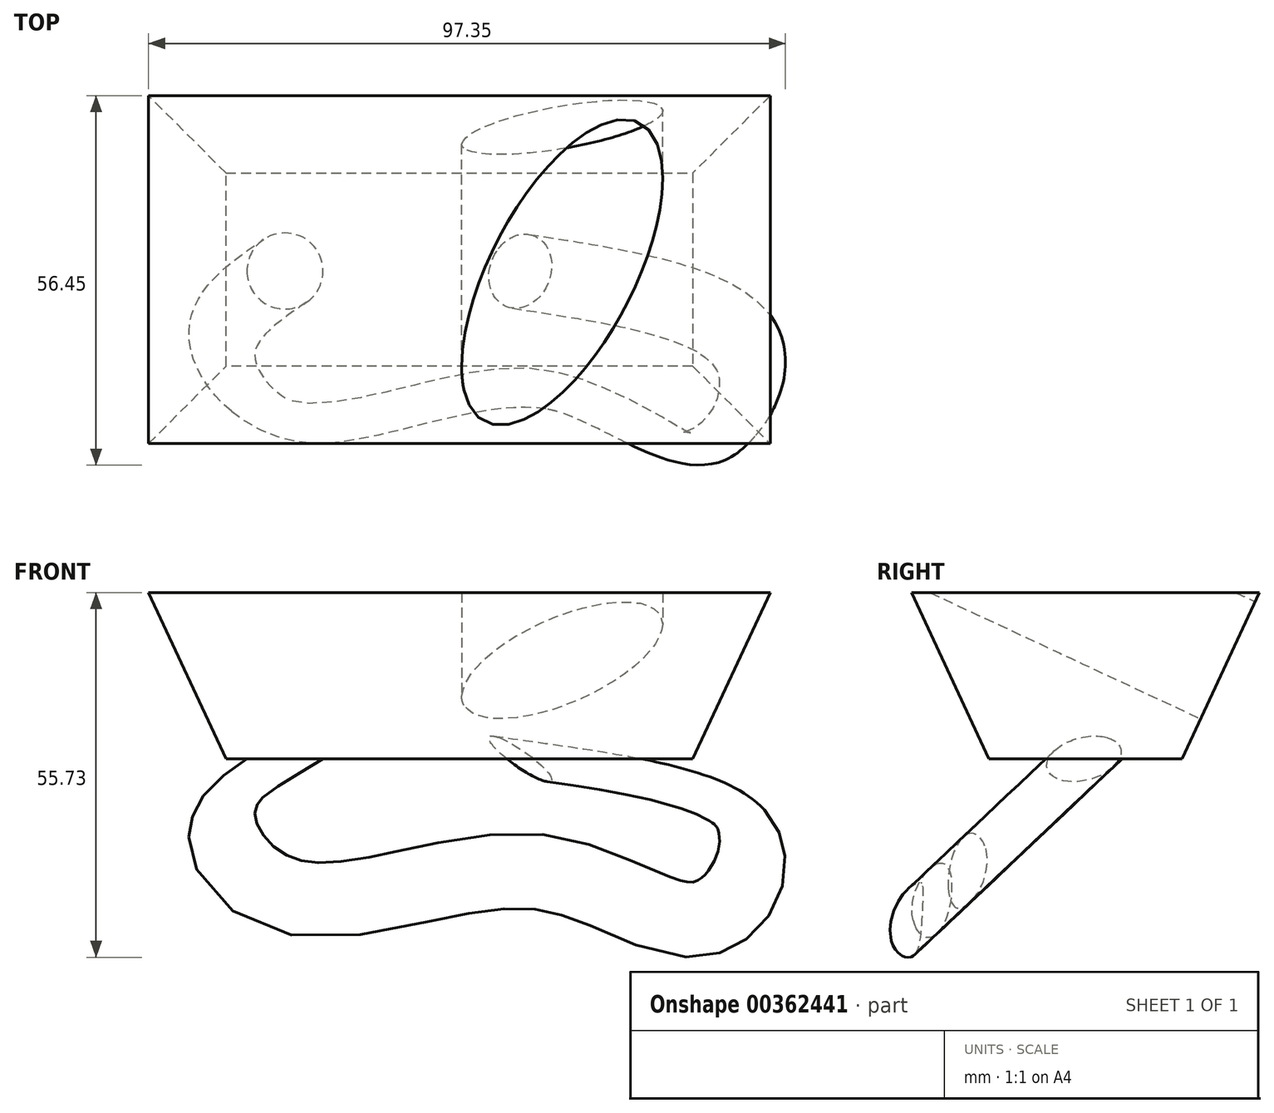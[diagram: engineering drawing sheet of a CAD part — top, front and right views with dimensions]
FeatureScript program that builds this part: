
annotation { "Feature Type Name" : "Feature", "Feature Type Description" : "" }
export const myFeature = defineFeature(function(context is Context, id is Id, definition is map)
    precondition{}
    {
        {
            var Q0;
            Q0=qCreatedBy(makeId("Top.planeOp"),FACE);
            var sketch = newSketch(context, id + "F0", { "sketchPlane" : qUnion([Q0])});
            skLineSegment(sketch, "E0.bottom", {"start": v(13.31, 11.56) * mm, "end": v(-58.01, 11.56) * mm});
            skLineSegment(sketch, "E0.top", {"start": v(13.31, 41.05) * mm, "end": v(-58.01, 41.05) * mm});
            skLineSegment(sketch, "E0.left", {"start": v(13.31, 11.56) * mm, "end": v(13.31, 41.05) * mm});
            skLineSegment(sketch, "E0.right", {"start": v(-58.01, 11.56) * mm, "end": v(-58.01, 41.05) * mm});
            skPoint(sketch, "E0.middle", {"position": v(-22.35, 26.3) * mm});
            skSolve(sketch);
        }
        {
            var Q0;
            Q0=makeQuery(id+"F0.imprint","IMPRINT",FACE,{"disambiguationData":[TD([[makeQuery(id+"F0.imprint","IMPRINT",EDGE,{"derivedFrom":sQuery(id+"F0.wireOp",EDGE,"E0.bottom")}),-1.0]])]});
            extrude(context, id + "F1", {"entities" : qUnion([Q0]), "depth" : 25.4 * mm, "hasDraft" : true, "draftAngle" : 25 * degree});
        }
        {
            var Q0;
            Q0=makeQuery(id+"F1.opExtrude","SWEPT_FACE",FACE,{"disambiguationData":[OSD([sQuery(id+"F0.wireOp",EDGE,"E0.top")])]});
            var sketch = newSketch(context, id + "F2", { "sketchPlane" : qUnion([Q0])});
            skEllipse(sketch, "E1", {"center": v(6.63, 33.97) * mm, "majorRadius": 16.83 * mm, "minorRadius": 7.1 * mm, "majorAxis": v(0.9, -0.45)});
            skSolve(sketch);
        }
        {
            var Q0;
            Q0=makeQuery(id+"F2.imprint","IMPRINT",FACE,{"disambiguationData":[TD([[makeQuery(id+"F2.imprint","IMPRINT",EDGE,{"derivedFrom":sQuery(id+"F2.wireOp",EDGE,"E1")}),1.0]])]});
            var Q1;
            Q1=sQuery(id+"F2.wireOp",EDGE,"E1");
            extrude(context, id + "F3", {"entities" : qUnion([Q0]), "operationType" : NewBodyOperationType.REMOVE, "surfaceEntities" : qUnion([Q1]), "endBound" : BoundingType.THROUGH_ALL, "oppositeDirection" : true, "depth" : 25.4 * mm});
        }
        {
            var Q0;
            Q0=makeQuery(id+"F1.opExtrude","CAP_FACE",FACE,{"disambiguationData":[OSD([sQuery(id+"F0.wireOp",EDGE,"E0.bottom"),sQuery(id+"F0.wireOp",EDGE,"E0.top"),sQuery(id+"F0.wireOp",EDGE,"E0.left"),sQuery(id+"F0.wireOp",EDGE,"E0.right")])],"isStart":false});
            var sketch = newSketch(context, id + "F4", { "sketchPlane" : qUnion([Q0])});
            skFitSpline(sketch, "E2", {"points": [v(-31.99, 19.24) * mm, v(-35.6, 14.59) * mm, v(-41.11, 14.23) * mm, v(-47.4, 17.12) * mm, v(-54.28, 21.87) * mm, v(-46.85, 24.59) * mm, v(-37.28, 24.56) * mm, v(-31.99, 19.24) * mm]});
            skSolve(sketch);
        }
        {
            var Q0;
            Q0=sQuery(id+"F4.wireOp",EDGE,"E2");
            extrude(context, id + "F5", {"bodyType" : ToolBodyType.SURFACE, "surfaceEntities" : qUnion([Q0]), "depth" : 47 * mm});
        }
        {
            var Q0;
            Q0=makeQuery(id+"F1.opExtrude","CAP_FACE",FACE,{"disambiguationData":[OSD([sQuery(id+"F0.wireOp",EDGE,"E0.bottom"),sQuery(id+"F0.wireOp",EDGE,"E0.top"),sQuery(id+"F0.wireOp",EDGE,"E0.left"),sQuery(id+"F0.wireOp",EDGE,"E0.right")])],"isStart":true});
            var sketch = newSketch(context, id + "F6", { "sketchPlane" : qUnion([Q0])});
            skCircle(sketch, "E3", {"center": v(-49, -26.1) * mm, "radius": 5.82 * mm});
            skCircle(sketch, "E4", {"center": v(-13.04, -26.07) * mm, "radius": 7.15 * mm});
            skSolve(sketch);
        }
        {
            var Q0;
            Q0=sQuery(id+"F6.wireOp",VERTEX,"E3.center");
            var Q1;
            Q1=sQuery(id+"F6.wireOp",VERTEX,"E4.center");
            var Q2;
            Q2=makeQuery(id+"F1.opExtrude","CAP_VERTEX",VERTEX,{"disambiguationData":[OSD([sQuery(id+"F0.wireOp",EDGE,"E0.top"),sQuery(id+"F0.wireOp",EDGE,"E0.left")])],"isStart":false});
            cPlane(context, id + "F7", {"entities" : qUnion([Q0, Q1, Q2]), "cplaneType" : CPlaneType.THREE_POINT, "offset" : 25.4 * mm, "width" : 152.4 * mm, "height" : 152.4 * mm});
        }
        {
            var Q0;
            Q0=qCreatedBy(id+"F7.planeOp",FACE);
            var sketch = newSketch(context, id + "F8", { "sketchPlane" : qUnion([Q0])});
            skPoint(sketch, "E5.0", {"position": v(-49.02, -18.97) * mm});
            skPoint(sketch, "E6.0", {"position": v(-13.05, -18.94) * mm});
            skFitSpline(sketch, "E7", {"points": [v(-49.02, -18.97) * mm, v(-58.56, -4.21) * mm, v(-46.43, 12.2) * mm, v(-10.22, 6.22) * mm, v(14.51, 16.7) * mm, v(21.63, -2.62) * mm, v(-13.05, -18.94) * mm], "startDerivative": vector(-102.38, 96.08) * mm, "endDerivative": vector(-232.43, -48.46) * mm});
            skSolve(sketch);
        }
        {
            var Q0;
            Q0=makeQuery(id+"F6.imprint","IMPRINT",FACE,{"disambiguationData":[TD([[makeQuery(id+"F6.imprint","IMPRINT",EDGE,{"derivedFrom":sQuery(id+"F6.wireOp",EDGE,"E3")}),1.0]])]});
            var Q1;
            Q1=sQuery(id+"F8.wireOp",EDGE,"E7");
            sweep(context, id + "F9", {"profiles" : qUnion([Q0]), "path" : qUnion([Q1])});
        }
    });
